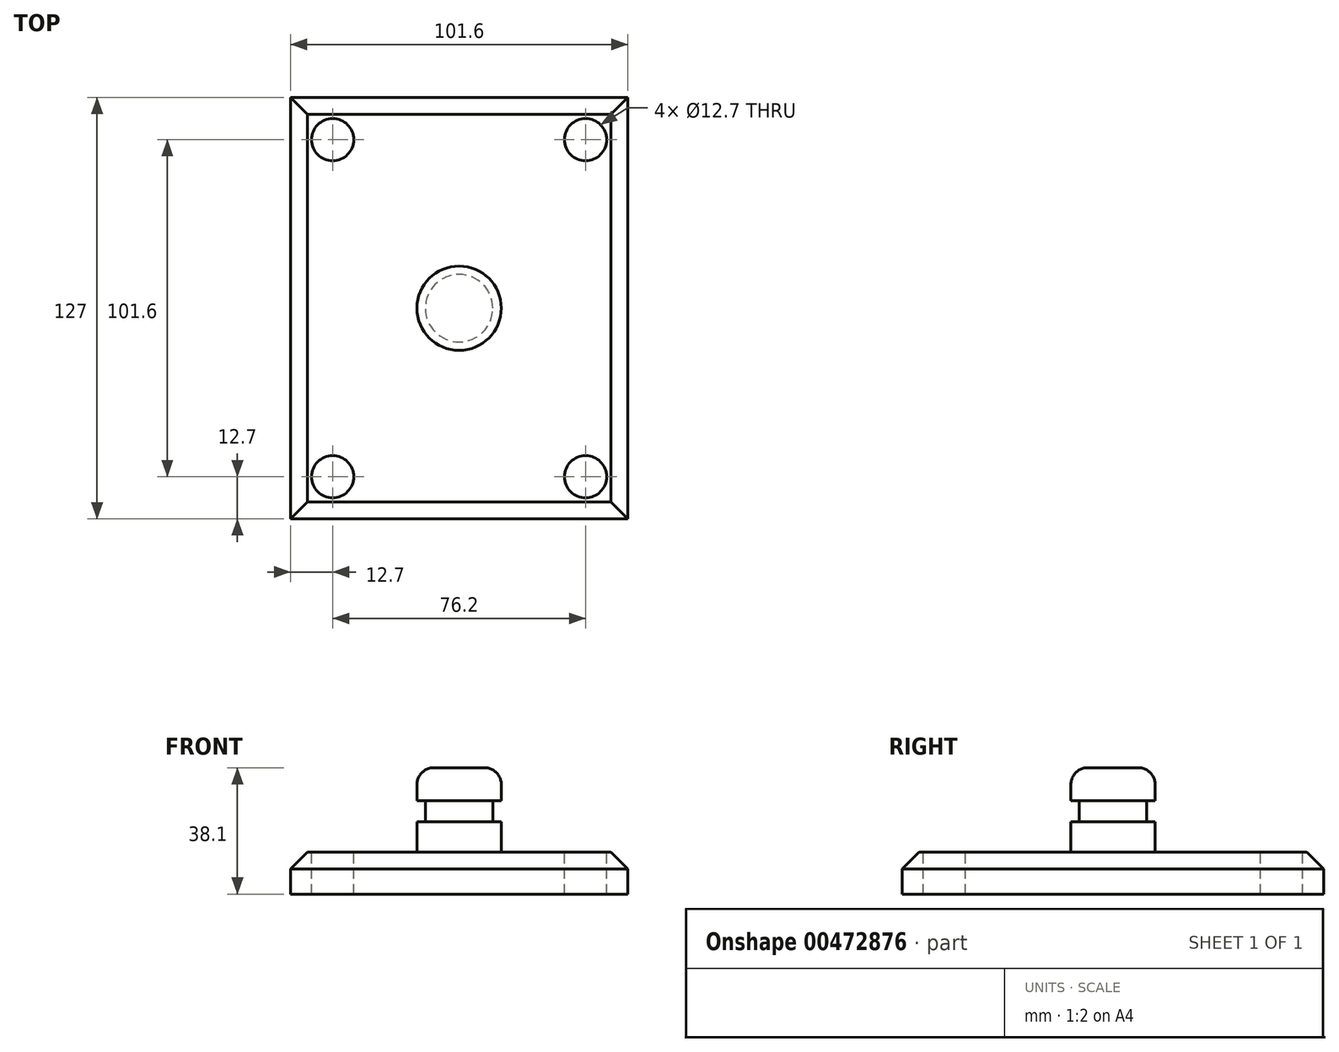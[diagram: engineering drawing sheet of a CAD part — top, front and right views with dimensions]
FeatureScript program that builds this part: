
annotation { "Feature Type Name" : "Feature", "Feature Type Description" : "" }
export const myFeature = defineFeature(function(context is Context, id is Id, definition is map)
    precondition{}
    {
        {
            var Q0;
            Q0=qCreatedBy(makeId("Top.planeOp"),FACE);
            var sketch = newSketch(context, id + "F0", { "sketchPlane" : qUnion([Q0])});
            skLineSegment(sketch, "E0.bottom", {"start": v(50.8, -63.5) * mm, "end": v(-50.8, -63.5) * mm});
            skLineSegment(sketch, "E0.top", {"start": v(50.8, 63.5) * mm, "end": v(-50.8, 63.5) * mm});
            skLineSegment(sketch, "E0.left", {"start": v(50.8, -63.5) * mm, "end": v(50.8, 63.5) * mm});
            skLineSegment(sketch, "E0.right", {"start": v(-50.8, -63.5) * mm, "end": v(-50.8, 63.5) * mm});
            skPoint(sketch, "E0.middle", {"position": v(0, 0) * mm});
            skSolve(sketch);
        }
        {
            var Q0;
            Q0=makeQuery(id+"F0.imprint","IMPRINT",FACE,{"disambiguationData":[TD([[makeQuery(id+"F0.imprint","IMPRINT",EDGE,{"derivedFrom":sQuery(id+"F0.wireOp",EDGE,"E0.bottom")}),-1.0]])]});
            extrude(context, id + "F1", {"entities" : qUnion([Q0]), "depth" : 12.7 * mm});
        }
        {
            var Q0;
            Q0=makeQuery(id+"F1.opExtrude","CAP_FACE",FACE,{"disambiguationData":[OSD([sQuery(id+"F0.wireOp",EDGE,"E0.bottom"),sQuery(id+"F0.wireOp",EDGE,"E0.top"),sQuery(id+"F0.wireOp",EDGE,"E0.left"),sQuery(id+"F0.wireOp",EDGE,"E0.right")])],"isStart":false});
            var sketch = newSketch(context, id + "F2", { "sketchPlane" : qUnion([Q0])});
            skCircle(sketch, "E1", {"center": v(-38.1, 50.8) * mm, "radius": 6.35 * mm});
            skCircle(sketch, "E2", {"center": v(38.1, 50.8) * mm, "radius": 6.35 * mm});
            skCircle(sketch, "E3", {"center": v(-38.1, -50.8) * mm, "radius": 6.35 * mm});
            skCircle(sketch, "E4", {"center": v(38.1, -50.8) * mm, "radius": 6.35 * mm});
            skSolve(sketch);
        }
        {
            var Q0;
            Q0 = qSketchRegion(id + "F2", true);
            var Q1;
            Q1=sQuery(id+"F2.wireOp",EDGE,"E3");
            extrude(context, id + "F3", {"entities" : qUnion([Q0]), "operationType" : NewBodyOperationType.REMOVE, "surfaceEntities" : qUnion([Q1]), "endBound" : BoundingType.THROUGH_ALL, "oppositeDirection" : true, "depth" : 25.4 * mm});
        }
        {
            var Q0;
            Q0=qCreatedBy(makeId("Front.planeOp"),FACE);
            var sketch = newSketch(context, id + "F4", { "sketchPlane" : qUnion([Q0])});
            skLineSegment(sketch, "E5.bottom", {"start": v(0, 12.7) * mm, "end": v(12.7, 12.7) * mm});
            skLineSegment(sketch, "E5.top", {"start": v(0, 38.1) * mm, "end": v(12.7, 38.1) * mm});
            skLineSegment(sketch, "E5.left", {"start": v(0, 12.7) * mm, "end": v(0, 38.1) * mm});
            skLineSegment(sketch, "E5.right", {"start": v(12.7, 12.7) * mm, "end": v(12.7, 38.1) * mm});
            skSolve(sketch);
        }
        {
            var Q0;
            Q0=makeQuery(id+"F4.imprint","IMPRINT",FACE,{"disambiguationData":[TD([[makeQuery(id+"F4.imprint","IMPRINT",EDGE,{"derivedFrom":sQuery(id+"F4.wireOp",EDGE,"E5.bottom")}),1.0]])]});
            var Q1;
            Q1=sQuery(id+"F4.wireOp",EDGE,"E5.left");
            revolve(context, id + "F5", {"operationType" : NewBodyOperationType.ADD, "entities" : qUnion([Q0]), "axis" : qUnion([Q1]), "revolveType" : RevolveType.FULL});
        }
        {
            var Q0;
            Q0=qCreatedBy(makeId("Front.planeOp"),FACE);
            var sketch = newSketch(context, id + "F6", { "sketchPlane" : qUnion([Q0])});
            skLineSegment(sketch, "E6.bottom", {"start": v(22.86, 28.16) * mm, "end": v(10.16, 28.16) * mm});
            skLineSegment(sketch, "E6.top", {"start": v(22.86, 21.81) * mm, "end": v(10.16, 21.81) * mm});
            skLineSegment(sketch, "E6.left", {"start": v(22.86, 28.16) * mm, "end": v(22.86, 21.81) * mm});
            skLineSegment(sketch, "E6.right", {"start": v(10.16, 28.16) * mm, "end": v(10.16, 21.81) * mm});
            skSolve(sketch);
        }
        {
            var Q0;
            Q0=makeQuery(id+"F6.imprint","IMPRINT",FACE,{"disambiguationData":[TD([[makeQuery(id+"F6.imprint","IMPRINT",EDGE,{"derivedFrom":sQuery(id+"F6.wireOp",EDGE,"E6.bottom")}),1.0]])]});
            var Q1;
            Q1=makeQuery(id+"F5.opRevolve","SWEPT_FACE",FACE,{"disambiguationData":[OSD([sQuery(id+"F4.wireOp",EDGE,"E5.right")])]});
            revolve(context, id + "F7", {"operationType" : NewBodyOperationType.REMOVE, "entities" : qUnion([Q0]), "axis" : qUnion([Q1]), "revolveType" : RevolveType.FULL, "oppositeDirection" : true});
        }
        {
            var Q0;
            Q0=makeQuery(id+"F5.opRevolve","SWEPT_EDGE",EDGE,{"disambiguationData":[OSD([sQuery(id+"F4.wireOp",EDGE,"E5.bottom"),sQuery(id+"F4.wireOp",EDGE,"E5.right")])]});
            var Q1;
            Q1=makeQuery(id+"F5.opRevolve","SWEPT_EDGE",EDGE,{"disambiguationData":[OSD([sQuery(id+"F4.wireOp",EDGE,"E5.top"),sQuery(id+"F4.wireOp",EDGE,"E5.right")])]});
            fillet(context, id + "F8", {"entities" : qUnion([Q0, Q1]), "radius" : 5.08 * mm, "tangentPropagation" : true, "allowEdgeOverflow" : false});
        }
        {
            var Q0;
            Q0=makeQuery(id+"F1.opExtrude","CAP_EDGE",EDGE,{"disambiguationData":[OSD([sQuery(id+"F0.wireOp",EDGE,"E0.right")])],"isStart":false});
            var Q1;
            Q1=makeQuery(id+"F1.opExtrude","CAP_EDGE",EDGE,{"disambiguationData":[OSD([sQuery(id+"F0.wireOp",EDGE,"E0.bottom")])],"isStart":false});
            var Q2;
            Q2=makeQuery(id+"F1.opExtrude","CAP_EDGE",EDGE,{"disambiguationData":[OSD([sQuery(id+"F0.wireOp",EDGE,"E0.top")])],"isStart":false});
            var Q3;
            Q3=makeQuery(id+"F1.opExtrude","CAP_EDGE",EDGE,{"disambiguationData":[OSD([sQuery(id+"F0.wireOp",EDGE,"E0.left")])],"isStart":false});
            chamfer(context, id + "F9", {"entities" : qUnion([Q0, Q1, Q2, Q3]), "chamferType" : ChamferType.TWO_OFFSETS, "width1" : 5.08 * mm, "oppositeDirection" : false, "width2" : 5.08 * mm, "tangentPropagation" : true});
        }
    });
